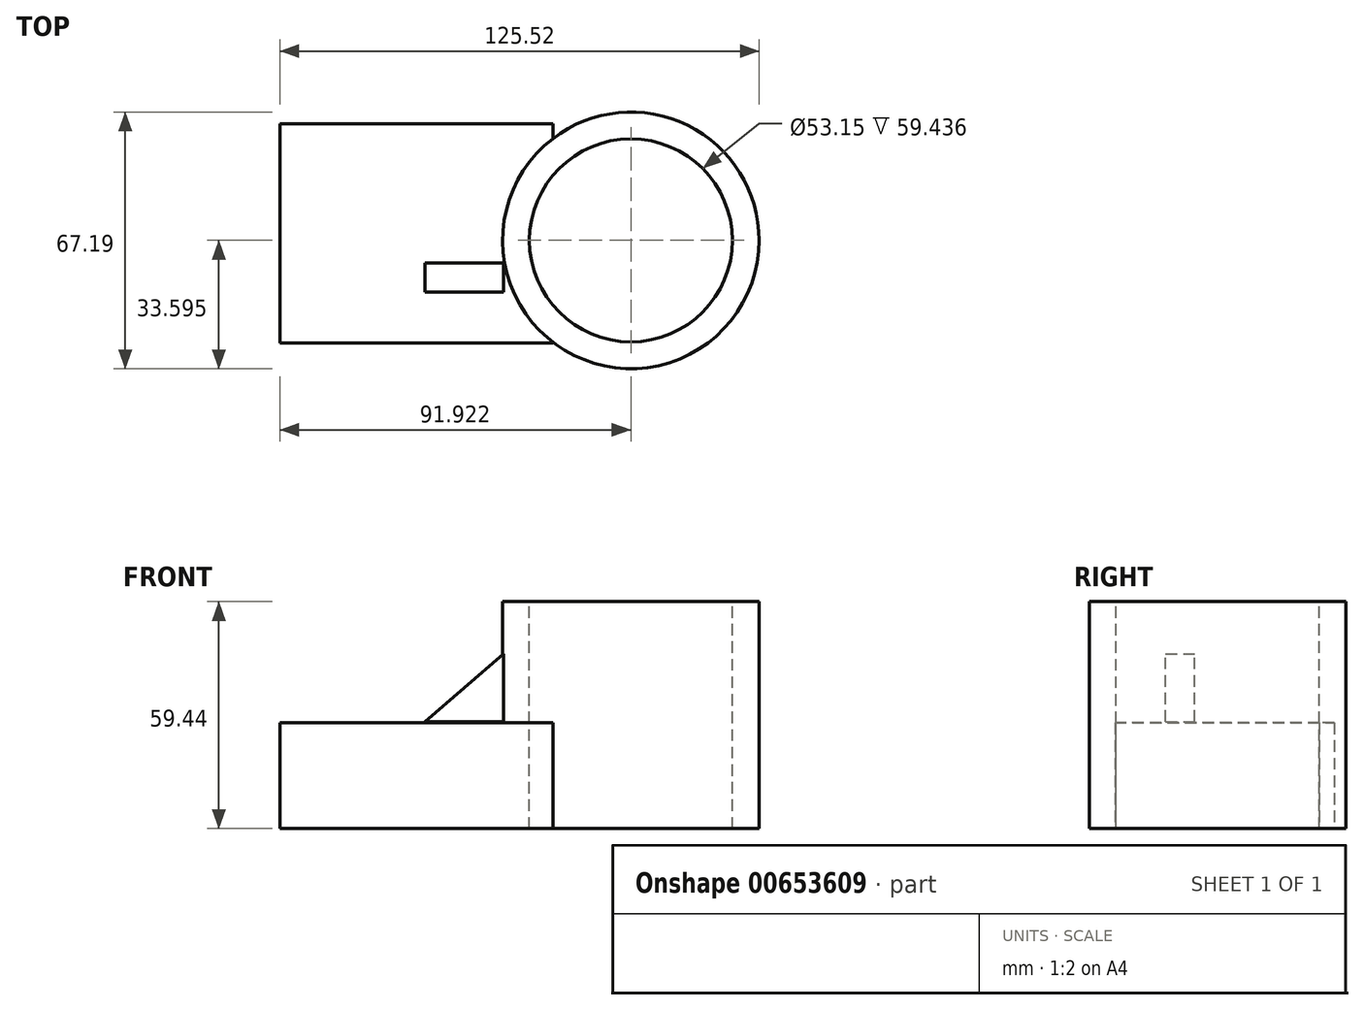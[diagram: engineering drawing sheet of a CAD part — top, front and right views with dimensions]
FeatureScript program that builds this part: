
annotation { "Feature Type Name" : "Feature", "Feature Type Description" : "" }
export const myFeature = defineFeature(function(context is Context, id is Id, definition is map)
    precondition{}
    {
        {
            var Q0;
            Q0=qCreatedBy(makeId("Top.planeOp"),FACE);
            var sketch = newSketch(context, id + "F0", { "sketchPlane" : qUnion([Q0])});
            skLineSegment(sketch, "E0", {"start": v(-56.04, 36.51) * mm, "end": v(15.42, 36.51) * mm});
            skLineSegment(sketch, "E1", {"start": v(15.42, 36.51) * mm, "end": v(15.42, -20.94) * mm});
            skLineSegment(sketch, "E2", {"start": v(15.42, -20.94) * mm, "end": v(-56.04, -20.94) * mm});
            skLineSegment(sketch, "E3", {"start": v(-56.04, -20.94) * mm, "end": v(-56.04, 36.51) * mm});
            skSolve(sketch);
        }
        {
            var Q0;
            Q0=makeQuery(id+"F0.imprint","IMPRINT",FACE,{"disambiguationData":[TD([[makeQuery(id+"F0.imprint","IMPRINT",EDGE,{"derivedFrom":sQuery(id+"F0.wireOp",EDGE,"E0")}),-1.0]])]});
            extrude(context, id + "F1", {"entities" : qUnion([Q0]), "depth" : 27.7 * mm, "offsetDistance" : 25.4 * mm});
        }
        {
            var Q0;
            Q0=qCreatedBy(makeId("Top.planeOp"),FACE);
            var sketch = newSketch(context, id + "F2", { "sketchPlane" : qUnion([Q0])});
            skCircle(sketch, "E4", {"center": v(35.88, 5.95) * mm, "radius": 33.6 * mm});
            skSolve(sketch);
        }
        {
            var Q0;
            Q0=makeQuery(id+"F2.imprint","IMPRINT",FACE,{"disambiguationData":[TD([[makeQuery(id+"F2.imprint","IMPRINT",EDGE,{"derivedFrom":sQuery(id+"F2.wireOp",EDGE,"E4")}),1.0]])]});
            extrude(context, id + "F3", {"entities" : qUnion([Q0]), "operationType" : NewBodyOperationType.ADD, "depth" : 59.44 * mm, "offsetDistance" : 25.4 * mm});
        }
        {
            var Q0;
            Q0=makeQuery(id+"F3.opExtrude","CAP_FACE",FACE,{"disambiguationData":[OSD([sQuery(id+"F2.wireOp",EDGE,"E4")])],"isStart":false});
            var sketch = newSketch(context, id + "F4", { "sketchPlane" : qUnion([Q0])});
            skCircle(sketch, "E5", {"center": v(35.88, 5.95) * mm, "radius": 26.58 * mm});
            skSolve(sketch);
        }
        {
            var Q0;
            Q0=makeQuery(id+"F4.imprint","IMPRINT",FACE,{"disambiguationData":[TD([[makeQuery(id+"F4.imprint","IMPRINT",EDGE,{"derivedFrom":sQuery(id+"F4.wireOp",EDGE,"E5")}),1.0]])]});
            extrude(context, id + "F5", {"entities" : qUnion([Q0]), "operationType" : NewBodyOperationType.REMOVE, "endBound" : BoundingType.SYMMETRIC, "oppositeDirection" : true, "depth" : 240.8 * mm, "offsetDistance" : 25.4 * mm});
        }
        {
            var Q0;
            Q0=qCreatedBy(makeId("Front.planeOp"),FACE);
            var sketch = newSketch(context, id + "F6", { "sketchPlane" : qUnion([Q0])});
            skLineSegment(sketch, "E6", {"start": v(-18.06, 27.97) * mm, "end": v(2.58, 45.72) * mm});
            skLineSegment(sketch, "E7", {"start": v(2.58, 45.72) * mm, "end": v(2.58, 27.97) * mm});
            skLineSegment(sketch, "E8", {"start": v(2.58, 27.97) * mm, "end": v(-18.06, 27.97) * mm});
            skSolve(sketch);
        }
        {
            var Q0;
            Q0=makeQuery(id+"F6.imprint","IMPRINT",FACE,{"disambiguationData":[TD([[makeQuery(id+"F6.imprint","IMPRINT",EDGE,{"derivedFrom":sQuery(id+"F6.wireOp",EDGE,"E6")}),-1.0]])]});
            extrude(context, id + "F7", {"entities" : qUnion([Q0]), "depth" : 7.62 * mm, "offsetDistance" : 25.4 * mm});
        }
    });
